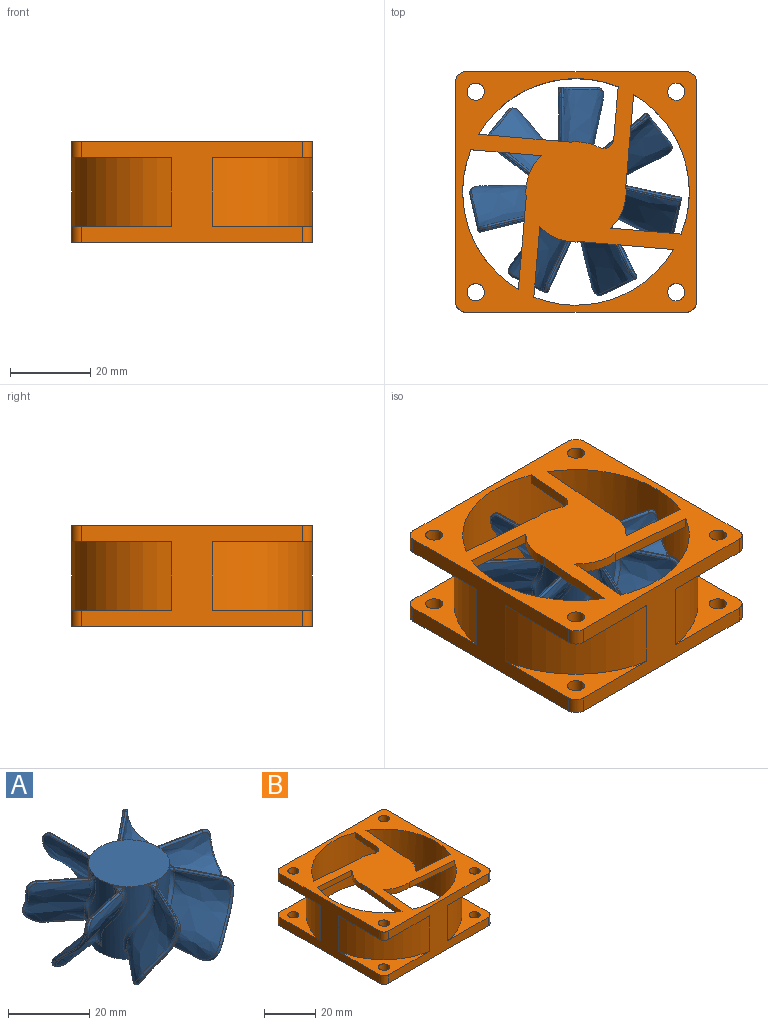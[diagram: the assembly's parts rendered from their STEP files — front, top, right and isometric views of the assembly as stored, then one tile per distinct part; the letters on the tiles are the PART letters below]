
ASSEMBLY  parts=2 mates=1
PART A: 199 faces, bbox 53.4x52.7x22.2 mm
  f0: cylinder r=10mm len=22mm, axis (0,0,-1), area 948.6mm2, adj f1,f2,f9,f10,f11,f12,f67,f68
  f1: plane 20x20mm, normal (0,0,1), area 314.2mm2, adj f0
  f2: plane 20x20mm, normal (0,0,-1), area 314.2mm2, adj f0
  f3: bspline ~20.21x17.68mm, area 299.4mm2, adj f10,f15,f18,f20,f21,f22,f24
  f4: extruded ~13.01x0.16mm, area 0.7mm2, adj f8,f12,f14,f15,f28
  f5: bspline ~20.23x18.05mm, area 308.2mm2, adj f11,f19,f23,f25,f26,f27,f28,f29
  f6: plane 11.67x8.91mm, normal (0,1,0), area 3.8mm2, adj f7,f8,f22,f26
  f7: cylinder r=5mm len=4.65mm, axis (-1,0,0), area 1mm2, adj f6,f24,f25
  f8: cylinder r=2.5mm len=2.52mm, axis (1,0,0), area 0.7mm2, adj f4,f6,f18,f27
  f9: bspline ~2.96x1.67mm, area 1.9mm2, adj f0,f16,f17
  f10: bspline ~20.09x7.77mm, area 29.9mm2, adj f0,f3,f13,f14,f17
  f11: bspline ~20.03x7.98mm, area 28mm2, adj f0,f5,f16,f30
  f12: bspline ~3.16x1.87mm, area 1.7mm2, adj f0,f4,f13,f29,f30
  f13: bspline ~1.99x1.62mm, area 0.7mm2, adj f10,f12,f14
  f14: bspline ~0.62x0.6mm, area 0.2mm2, adj f4,f10,f13,f15
  f15: bspline ~12.73x0.83mm, area 10.9mm2, adj f3,f4,f14,f18
  f16: bspline ~1.89x1.59mm, area 1.1mm2, adj f9,f11,f17,f19,f20
  f17: bspline ~1.38x1.23mm, area 0.7mm2, adj f9,f10,f16,f20
  f18: bspline ~2.52x2.5mm, area 2.9mm2, adj f3,f8,f15,f22
  f19: cylinder r=0.5mm len=0.55mm, axis (-0.21,-0.97,0.07), area 0mm2, adj f5,f16,f20,f23
  f20: bspline ~0.53x0.48mm, area 0.2mm2, adj f3,f16,f17,f19,f21,f23
  f21: bspline ~9.82x2.59mm, area 7.4mm2, adj f3,f20,f23,f24
  f22: bspline ~11.71x9.04mm, area 11.6mm2, adj f3,f6,f18,f24
  f23: bspline ~9.93x2.63mm, area 8.1mm2, adj f5,f19,f20,f21,f24,f25
  f24: bspline ~5.91x5.37mm, area 7.8mm2, adj f3,f7,f21,f22,f23,f25
  f25: bspline ~5.79x5.01mm, area 5.9mm2, adj f5,f7,f23,f24,f26
  f26: bspline ~11.99x9.12mm, area 12mm2, adj f5,f6,f25,f27
  f27: bspline ~2.53x2.52mm, area 2.7mm2, adj f5,f8,f26,f28
  f28: bspline ~13.02x0.64mm, area 8.3mm2, adj f4,f5,f27,f29
  f29: bspline ~0.64x0.48mm, area 0.3mm2, adj f5,f12,f28,f30
  f30: bspline ~1.24x0.96mm, area 0.3mm2, adj f11,f12,f29
  f31: bspline ~20.48x20.21mm, area 299.4mm2, adj f68,f93,f96,f98,f99,f100,f102
  f32: extruded ~10.27x8.24mm, area 0.7mm2, adj f61,f70,f92,f93,f106
  f33: bspline ~20.8x20.23mm, area 308.2mm2, adj f69,f97,f101,f103,f104,f105,f106,f107
  f34: plane 11.67x6.97mm, normal (0.78,0.62,0), area 3.8mm2, adj f55,f61,f100,f104
  f35: bspline ~20.21x18.8mm, area 299.4mm2, adj f72,f111,f114,f116,f117,f118,f120
  f36: extruded ~12.72x3.05mm, area 0.7mm2, adj f62,f74,f110,f111,f124
  f37: bspline ~20.23x19.2mm, area 308.2mm2, adj f73,f115,f119,f121,f122,f123,f124,f125
  f38: plane 11.67x8.69mm, normal (0.97,-0.22,0), area 3.8mm2, adj f56,f62,f118,f122
  f39: bspline ~20.56x20.21mm, area 299.4mm2, adj f76,f129,f132,f134,f135,f136,f138
  f40: extruded ~11.79x5.79mm, area 0.7mm2, adj f63,f78,f128,f129,f142
  f41: bspline ~20.92x20.23mm, area 308.2mm2, adj f77,f133,f137,f139,f140,f141,f142,f143
  f42: plane 11.67x8.03mm, normal (0.43,-0.9,0), area 3.8mm2, adj f57,f63,f136,f140
  f43: bspline ~20.21x18.97mm, area 299.4mm2, adj f80,f147,f150,f152,f153,f154,f156
  f44: extruded ~11.79x5.79mm, area 0.7mm2, adj f64,f82,f146,f147,f160
  f45: bspline ~20.23x19.39mm, area 308.2mm2, adj f81,f151,f155,f157,f158,f159,f160,f161
  f46: plane 11.67x8.03mm, normal (-0.43,-0.9,0), area 3.8mm2, adj f58,f64,f154,f158
  f47: bspline ~20.21x19.62mm, area 299.4mm2, adj f84,f165,f168,f170,f171,f172,f174
  f48: extruded ~12.72x3.05mm, area 0.7mm2, adj f65,f86,f164,f165,f178
  f49: bspline ~20.23x19.99mm, area 308.2mm2, adj f85,f169,f173,f175,f176,f177,f178,f179
  f50: plane 11.67x8.69mm, normal (-0.97,-0.22,0), area 3.8mm2, adj f59,f65,f172,f176
  f51: bspline ~20.21x19.37mm, area 299.4mm2, adj f88,f183,f186,f188,f189,f190,f192
  f52: extruded ~10.27x8.24mm, area 0.7mm2, adj f66,f90,f182,f183,f196
  f53: bspline ~20.23x19.64mm, area 308.2mm2, adj f89,f187,f191,f193,f194,f195,f196,f197
  f54: plane 11.67x6.97mm, normal (-0.78,0.62,0), area 3.8mm2, adj f60,f66,f190,f194
  f55: cylinder r=5mm len=4.65mm, axis (-0.62,0.78,0), area 1mm2, adj f34,f102,f103
  f56: cylinder r=5mm len=4.65mm, axis (0.22,0.97,0), area 1mm2, adj f38,f120,f121
  f57: cylinder r=5mm len=4.65mm, axis (0.9,0.43,0), area 1mm2, adj f42,f138,f139
  f58: cylinder r=5mm len=4.65mm, axis (0.9,-0.43,0), area 1mm2, adj f46,f156,f157
  f59: cylinder r=5mm len=4.65mm, axis (0.22,-0.97,0), area 1mm2, adj f50,f174,f175
  f60: cylinder r=5mm len=4.65mm, axis (-0.62,-0.78,0), area 1mm2, adj f54,f192,f193
  f61: cylinder r=2.5mm len=2.5mm, axis (0.62,-0.78,0), area 0.7mm2, adj f32,f34,f96,f105
  f62: cylinder r=2.5mm len=2.54mm, axis (-0.22,-0.97,0), area 0.7mm2, adj f36,f38,f114,f123
  f63: cylinder r=2.5mm len=2.5mm, axis (-0.9,-0.43,0), area 0.7mm2, adj f40,f42,f132,f141
  f64: cylinder r=2.5mm len=2.5mm, axis (-0.9,0.43,0), area 0.7mm2, adj f44,f46,f150,f159
  f65: cylinder r=2.5mm len=2.54mm, axis (-0.22,0.97,0), area 0.7mm2, adj f48,f50,f168,f177
  f66: cylinder r=2.5mm len=2.5mm, axis (0.62,0.78,0), area 0.7mm2, adj f52,f54,f186,f195
  f67: bspline ~3.01x1.75mm, area 1.9mm2, adj f0,f94,f95
  f68: bspline ~20.09x7.25mm, area 29.9mm2, adj f0,f31,f91,f92,f95
  f69: bspline ~20.03x6.39mm, area 28mm2, adj f0,f33,f94,f108
  f70: bspline ~3.04x2.53mm, area 1.7mm2, adj f0,f32,f91,f107,f108
  f71: bspline ~2.86x2.19mm, area 1.9mm2, adj f0,f112,f113
  f72: bspline ~20.09x7.43mm, area 29.9mm2, adj f0,f35,f109,f110,f113
  f73: bspline ~19.77x8.16mm, area 28mm2, adj f0,f37,f112,f126
  f74: bspline ~3.12x1.33mm, area 1.7mm2, adj f0,f36,f109,f125,f126
  f75: bspline ~2.99x1.17mm, area 1.9mm2, adj f0,f130,f131
  f76: bspline ~20.09x7.82mm, area 29.9mm2, adj f0,f39,f127,f128,f131
  f77: bspline ~20.03x6.66mm, area 28mm2, adj f0,f41,f130,f144
  f78: bspline ~2.87x2.78mm, area 1.7mm2, adj f0,f40,f127,f143,f144
  f79: bspline ~2.61x2.6mm, area 1.9mm2, adj f0,f148,f149
  f80: bspline ~20.09x6.72mm, area 29.9mm2, adj f0,f43,f145,f146,f149
  f81: bspline ~20.03x7.97mm, area 28mm2, adj f0,f45,f148,f162
  f82: bspline ~3.09x1.49mm, area 1.7mm2, adj f0,f44,f145,f161,f162
  f83: bspline ~2.97x1.08mm, area 1.9mm2, adj f0,f166,f167
  f84: bspline ~20.09x8mm, area 29.9mm2, adj f0,f47,f163,f164,f167
  f85: bspline ~20.03x7.4mm, area 28mm2, adj f0,f49,f166,f180
  f86: bspline ~3.11x2.4mm, area 1.7mm2, adj f0,f48,f163,f179,f180
  f87: bspline ~2.87x2.24mm, area 1.9mm2, adj f0,f184,f185
  f88: bspline ~20.09x6.32mm, area 29.9mm2, adj f0,f51,f181,f182,f185
  f89: bspline ~20.03x7.37mm, area 28mm2, adj f0,f53,f184,f198
  f90: bspline ~3.15x2.06mm, area 1.7mm2, adj f0,f52,f181,f197,f198
  f91: bspline ~1.93x1.62mm, area 0.7mm2, adj f68,f70,f92
  f92: bspline ~0.6x0.59mm, area 0.2mm2, adj f32,f68,f91,f93
  f93: bspline ~10.27x8.44mm, area 10.9mm2, adj f31,f32,f92,f96
  f94: bspline ~1.64x1.59mm, area 1.1mm2, adj f67,f69,f95,f97,f98
  f95: bspline ~1.42x1.38mm, area 0.7mm2, adj f67,f68,f94,f98
  f96: bspline ~2.5x2.22mm, area 2.9mm2, adj f31,f61,f93,f100
  f97: cylinder r=0.5mm len=0.55mm, axis (-0.89,-0.44,0.07), area 0mm2, adj f33,f94,f98,f101
  f98: bspline ~0.59x0.49mm, area 0.2mm2, adj f31,f94,f95,f97,f99,f101
  f99: bspline ~9.2x4.83mm, area 7.4mm2, adj f31,f98,f101,f102
  f100: bspline ~11.71x7.38mm, area 11.6mm2, adj f31,f34,f96,f102
  f101: bspline ~9.17x4.93mm, area 8.1mm2, adj f33,f97,f98,f99,f102,f103
  f102: bspline ~5.37x4.9mm, area 7.8mm2, adj f31,f55,f99,f100,f101,f103
  f103: bspline ~5.01x4.76mm, area 5.9mm2, adj f33,f55,f101,f102,f104
  f104: bspline ~11.99x7.13mm, area 12mm2, adj f33,f34,f103,f105
  f105: bspline ~2.52x2.21mm, area 2.7mm2, adj f33,f61,f104,f106
  f106: bspline ~10.39x8.57mm, area 8.3mm2, adj f32,f33,f105,f107
  f107: bspline ~0.76x0.65mm, area 0.3mm2, adj f33,f70,f106,f108
  f108: bspline ~1.24x1.14mm, area 0.3mm2, adj f69,f70,f107
  f109: bspline ~1.82x1.62mm, area 0.7mm2, adj f72,f74,f110
  f110: bspline ~0.62x0.6mm, area 0.2mm2, adj f36,f72,f109,f111
  f111: bspline ~12.55x3.33mm, area 10.9mm2, adj f35,f36,f110,f114
  f112: bspline ~1.98x1.59mm, area 1.1mm2, adj f71,f73,f113,f115,f116
  f113: bspline ~1.39x1.38mm, area 0.7mm2, adj f71,f72,f112,f116
  f114: bspline ~2.61x2.5mm, area 2.9mm2, adj f35,f62,f111,f118
  f115: cylinder r=0.5mm len=0.55mm, axis (-0.9,0.42,0.07), area 0mm2, adj f37,f112,f116,f119
  f116: bspline ~0.56x0.53mm, area 0.2mm2, adj f35,f112,f113,f115,f117,f119
  f117: bspline ~9.2x4.68mm, area 7.4mm2, adj f35,f116,f119,f120
  f118: bspline ~11.71x8.81mm, area 11.6mm2, adj f35,f38,f114,f120
  f119: bspline ~9.32x4.7mm, area 8.1mm2, adj f37,f115,f116,f117,f120,f121
  f120: bspline ~6.02x5.37mm, area 7.8mm2, adj f35,f56,f117,f118,f119,f121
  f121: bspline ~5.97x5.01mm, area 5.9mm2, adj f37,f56,f119,f120,f122
  f122: bspline ~11.99x9mm, area 12mm2, adj f37,f38,f121,f123
  f123: bspline ~2.64x2.52mm, area 2.7mm2, adj f37,f62,f122,f124
  f124: bspline ~12.82x3.25mm, area 8.3mm2, adj f36,f37,f123,f125
  f125: bspline ~0.64x0.56mm, area 0.3mm2, adj f37,f74,f124,f126
  f126: bspline ~1.24x0.83mm, area 0.3mm2, adj f73,f74,f125
  f127: bspline ~2.05x1.62mm, area 0.7mm2, adj f76,f78,f128
  f128: bspline ~0.63x0.6mm, area 0.2mm2, adj f40,f76,f127,f129
  f129: bspline ~11.69x6.1mm, area 10.9mm2, adj f39,f40,f128,f132
  f130: bspline ~1.59x1.49mm, area 1.1mm2, adj f75,f77,f131,f133,f134
  f131: bspline ~1.38x1.28mm, area 0.7mm2, adj f75,f76,f130,f134
  f132: bspline ~2.5x2.45mm, area 2.9mm2, adj f39,f63,f129,f136
  f133: cylinder r=0.5mm len=0.55mm, axis (-0.23,0.97,0.07), area 0mm2, adj f41,f130,f134,f137
  f134: bspline ~0.56x0.48mm, area 0.2mm2, adj f39,f130,f131,f133,f135,f137
  f135: bspline ~9.87x2.78mm, area 7.4mm2, adj f39,f134,f137,f138
  f136: bspline ~11.71x8.35mm, area 11.6mm2, adj f39,f42,f132,f138
  f137: bspline ~9.82x2.86mm, area 8.1mm2, adj f41,f133,f134,f135,f138,f139
  f138: bspline ~5.43x5.37mm, area 7.8mm2, adj f39,f57,f135,f136,f137,f139
  f139: bspline ~5.07x5.01mm, area 5.9mm2, adj f41,f57,f137,f138,f140
  f140: bspline ~11.99x8.22mm, area 12mm2, adj f41,f42,f139,f141
  f141: bspline ~2.52x2.35mm, area 2.7mm2, adj f41,f63,f140,f142
  f142: bspline ~11.87x6.18mm, area 8.3mm2, adj f40,f41,f141,f143
  f143: bspline ~0.75x0.61mm, area 0.3mm2, adj f41,f78,f142,f144
  f144: bspline ~1.24x1.14mm, area 0.3mm2, adj f77,f78,f143
  f145: bspline ~1.62x1.57mm, area 0.7mm2, adj f80,f82,f146
  f146: bspline ~0.63x0.6mm, area 0.2mm2, adj f44,f80,f145,f147
  f147: bspline ~11.74x5.99mm, area 10.9mm2, adj f43,f44,f146,f150
  f148: bspline ~1.96x1.59mm, area 1.1mm2, adj f79,f81,f149,f151,f152
  f149: bspline ~1.47x1.38mm, area 0.7mm2, adj f79,f80,f148,f152
  f150: bspline ~2.56x2.5mm, area 2.9mm2, adj f43,f64,f147,f154
  f151: cylinder r=0.5mm len=0.55mm, axis (0.61,0.78,0.07), area 0mm2, adj f45,f148,f152,f155
  f152: bspline ~0.58x0.57mm, area 0.2mm2, adj f43,f148,f149,f151,f153,f155
  f153: bspline ~8.12x6.54mm, area 7.4mm2, adj f43,f152,f155,f156
  f154: bspline ~11.71x8.14mm, area 11.6mm2, adj f43,f46,f150,f156
  f155: bspline ~8.25x6.55mm, area 8.1mm2, adj f45,f151,f152,f153,f156,f157
  f156: bspline ~5.85x5.37mm, area 7.8mm2, adj f43,f58,f153,f154,f155,f157
  f157: bspline ~5.85x5.01mm, area 5.9mm2, adj f45,f58,f155,f156,f158
  f158: bspline ~11.99x8.43mm, area 12mm2, adj f45,f46,f157,f159
  f159: bspline ~2.63x2.52mm, area 2.7mm2, adj f45,f64,f158,f160
  f160: bspline ~11.98x5.97mm, area 8.3mm2, adj f44,f45,f159,f161
  f161: bspline ~0.66x0.62mm, area 0.3mm2, adj f45,f82,f160,f162
  f162: bspline ~1.24x0.98mm, area 0.3mm2, adj f81,f82,f161
  f163: bspline ~2.07x1.62mm, area 0.7mm2, adj f84,f86,f164
  f164: bspline ~0.64x0.6mm, area 0.2mm2, adj f48,f84,f163,f165
  f165: bspline ~12.52x3.46mm, area 10.9mm2, adj f47,f48,f164,f168
  f166: bspline ~1.72x1.59mm, area 1.1mm2, adj f83,f85,f167,f169,f170
  f167: bspline ~1.38x1.08mm, area 0.7mm2, adj f83,f84,f166,f170
  f168: bspline ~2.55x2.5mm, area 2.9mm2, adj f47,f65,f165,f172
  f169: cylinder r=0.5mm len=0.55mm, axis (1,0.01,0.07), area 0mm2, adj f49,f166,f170,f173
  f170: bspline ~0.49x0.48mm, area 0.2mm2, adj f47,f166,f167,f169,f171,f173
  f171: bspline ~10.04x1.81mm, area 7.4mm2, adj f47,f170,f173,f174
  f172: bspline ~11.71x8.9mm, area 11.6mm2, adj f47,f50,f168,f174
  f173: bspline ~10.04x1.9mm, area 8.1mm2, adj f49,f169,f170,f171,f174,f175
  f174: bspline ~5.71x5.37mm, area 7.8mm2, adj f47,f59,f171,f172,f173,f175
  f175: bspline ~5.47x5.01mm, area 5.9mm2, adj f49,f59,f173,f174,f176
  f176: bspline ~11.99x8.89mm, area 12mm2, adj f49,f50,f175,f177
  f177: bspline ~2.52x2.5mm, area 2.7mm2, adj f49,f65,f176,f178
  f178: bspline ~12.75x3.47mm, area 8.3mm2, adj f48,f49,f177,f179
  f179: bspline ~0.71x0.55mm, area 0.3mm2, adj f49,f86,f178,f180
  f180: bspline ~1.24x1.07mm, area 0.3mm2, adj f85,f86,f179
  f181: bspline ~1.71x1.62mm, area 0.7mm2, adj f88,f90,f182
  f182: bspline ~0.62x0.6mm, area 0.2mm2, adj f52,f88,f181,f183
  f183: bspline ~10.35x8.34mm, area 10.9mm2, adj f51,f52,f182,f186
  f184: bspline ~1.85x1.59mm, area 1.1mm2, adj f87,f89,f185,f187,f188
  f185: bspline ~1.48x1.38mm, area 0.7mm2, adj f87,f88,f184,f188
  f186: bspline ~2.5x2.39mm, area 2.9mm2, adj f51,f66,f183,f190
  f187: cylinder r=0.5mm len=0.55mm, axis (0.63,-0.77,0.07), area 0mm2, adj f53,f184,f188,f191
  f188: bspline ~0.6x0.54mm, area 0.2mm2, adj f51,f184,f185,f187,f189,f191
  f189: bspline ~8.07x6.64mm, area 7.4mm2, adj f51,f188,f191,f192
  f190: bspline ~11.71x7.07mm, area 11.6mm2, adj f51,f54,f186,f192
  f191: bspline ~8.06x6.76mm, area 8.1mm2, adj f53,f187,f188,f189,f192,f193
  f192: bspline ~5.39x5.37mm, area 7.8mm2, adj f51,f60,f189,f190,f191,f193
  f193: bspline ~5.44x5.01mm, area 5.9mm2, adj f53,f60,f191,f192,f194
  f194: bspline ~11.99x7.44mm, area 12mm2, adj f53,f54,f193,f195
  f195: bspline ~2.52x2.48mm, area 2.7mm2, adj f53,f66,f194,f196
  f196: bspline ~10.54x8.39mm, area 8.3mm2, adj f52,f53,f195,f197
  f197: bspline ~0.73x0.65mm, area 0.3mm2, adj f53,f90,f196,f198
  f198: bspline ~1.24x1.09mm, area 0.3mm2, adj f89,f90,f197
PART B: 49 faces, bbox 60x60x25 mm
  f0: cylinder r=2.15mm len=4.3mm, axis (0,0,-1), area 54mm2, adj f29,f33
  f1: cylinder r=2.15mm len=4.3mm, axis (0,0,-1), area 54mm2, adj f30,f33
  f2: cylinder r=2.15mm len=4.3mm, axis (0,0,-1), area 54mm2, adj f31,f33
  f3: cylinder r=2.15mm len=4.3mm, axis (0,0,-1), area 54mm2, adj f32,f33
  f4: cylinder r=28.25mm len=56.5mm, axis (0,0,-1), area 4394.5mm2, adj f16,f33,f38,f39,f40,f42,f43,f44
  f5: cylinder r=2.15mm len=4.3mm, axis (0,0,-1), area 54mm2, adj f15,f16
  f6: cylinder r=2.15mm len=4.3mm, axis (0,0,-1), area 54mm2, adj f14,f16
  f7: cylinder r=2.15mm len=4.3mm, axis (0,0,-1), area 54mm2, adj f13,f16
  f8: cylinder r=2.15mm len=4.3mm, axis (0,0,-1), area 54mm2, adj f12,f16
  f9: cylinder r=12.5mm len=10.43mm, axis (0,0,-1), area 28.7mm2, adj f33,f40,f45,f46
  f10: cylinder r=12.5mm len=10.43mm, axis (0,0,-1), area 28.7mm2, adj f33,f40,f43,f44
  f11: cylinder r=12.5mm len=10.43mm, axis (0,0,-1), area 28.7mm2, adj f33,f38,f40,f42
  f12: plane 25x25mm, normal (0,0,1), area 160.4mm2, adj f8,f22,f23,f24,f28
  f13: plane 25x25mm, normal (0,0,1), area 160.4mm2, adj f7,f20,f21,f22,f27
  f14: plane 25x25mm, normal (0,0,1), area 160.4mm2, adj f6,f18,f19,f20,f26
  f15: plane 25x25mm, normal (0,0,1), area 160.4mm2, adj f5,f17,f18,f24,f25
  f16: plane 60x60mm, normal (0,0,-1), area 1029.4mm2, adj f4,f5,f6,f7,f8,f17,f18,f19
  f17: cylinder r=2.5mm len=4mm, axis (0,0,-1), area 15.7mm2, adj f15,f16,f18,f24
  f18: plane 55x25mm, normal (0,-1,0), area 610mm2, adj f14,f15,f16,f17,f19,f25,f26,f29
  f19: cylinder r=2.5mm len=4mm, axis (0,0,-1), area 15.7mm2, adj f14,f16,f18,f20
  f20: plane 55x25mm, normal (1,0,0), area 610mm2, adj f13,f14,f16,f19,f21,f26,f27,f30
  f21: cylinder r=2.5mm len=4mm, axis (0,0,-1), area 15.7mm2, adj f13,f16,f20,f22
  f22: plane 55x25mm, normal (0,1,0), area 610mm2, adj f12,f13,f16,f21,f23,f27,f28,f31
  f23: cylinder r=2.5mm len=4mm, axis (0,0,-1), area 15.7mm2, adj f12,f16,f22,f24
  f24: plane 55x25mm, normal (-1,0,0), area 610mm2, adj f12,f15,f16,f17,f23,f25,f28,f29
  f25: cylinder r=30.41mm len=25mm, axis (0,0,-1), area 641.4mm2, adj f15,f18,f24,f29
  f26: cylinder r=30.41mm len=25mm, axis (0,0,-1), area 641.4mm2, adj f14,f18,f20,f30
  f27: cylinder r=30.41mm len=25mm, axis (0,0,-1), area 641.4mm2, adj f13,f20,f22,f31
  f28: cylinder r=30.41mm len=25mm, axis (0,0,-1), area 641.4mm2, adj f12,f22,f24,f32
  f29: plane 25x25mm, normal (0,0,-1), area 160.4mm2, adj f0,f18,f24,f25,f34
  f30: plane 25x25mm, normal (0,0,-1), area 160.4mm2, adj f1,f18,f20,f26,f35
  f31: plane 25x25mm, normal (0,0,-1), area 160.4mm2, adj f2,f20,f22,f27,f36
  f32: plane 25x25mm, normal (0,0,-1), area 160.4mm2, adj f3,f22,f24,f28,f37
  f33: plane 60x60mm, normal (0,0,1), area 1836.1mm2, adj f0,f1,f2,f3,f4,f9,f10,f11
  f34: cylinder r=2.5mm len=4mm, axis (0,0,-1), area 15.7mm2, adj f18,f24,f29,f33
  f35: cylinder r=2.5mm len=4mm, axis (0,0,-1), area 15.7mm2, adj f18,f20,f30,f33
  f36: cylinder r=2.5mm len=4mm, axis (0,0,-1), area 15.7mm2, adj f20,f22,f31,f33
  f37: cylinder r=2.5mm len=4mm, axis (0,0,-1), area 15.7mm2, adj f22,f24,f32,f33
  f38: plane 22.91x2.5mm, normal (1,-0.08,0), area 57.5mm2, adj f4,f11,f33,f40
  f39: plane 13.12x2.5mm, normal (-1,0.08,0), area 32.9mm2, adj f4,f33,f40,f48
  f40: plane 52.44x52.44mm, normal (0,0,-1), area 806.7mm2, adj f4,f9,f10,f11,f38,f39,f41,f42
  f41: cylinder r=12.5mm len=7.17mm, axis (0,0,-1), area 18.5mm2, adj f33,f40,f47,f48
  f42: plane 17.57x2.5mm, normal (0.08,1,0), area 44.1mm2, adj f4,f11,f33,f40
  f43: plane 22.91x2.5mm, normal (-0.08,-1,0), area 57.5mm2, adj f4,f10,f33,f40
  f44: plane 17.57x2.5mm, normal (1,-0.08,0), area 44.1mm2, adj f4,f10,f33,f40
  f45: plane 22.91x2.5mm, normal (-1,0.08,0), area 57.5mm2, adj f4,f9,f33,f40
  f46: plane 17.57x2.5mm, normal (-0.08,-1,0), area 44.1mm2, adj f4,f9,f33,f40
  f47: plane 22.91x2.5mm, normal (0.08,1,0), area 57.5mm2, adj f4,f33,f40,f41
  f48: cylinder r=2.5mm len=3.64mm, axis (0,0,-1), area 12.3mm2, adj f33,f39,f40,f41
PLACE A t=(-17.72,-2.62,-0.62)mm
PLACE B t=(-17.76,-2.67,-1.12)mm
MATE fastened A.f0 <-> B.f40  axis (0,0,1) through (-17.72,-2.62,21.38)mm
